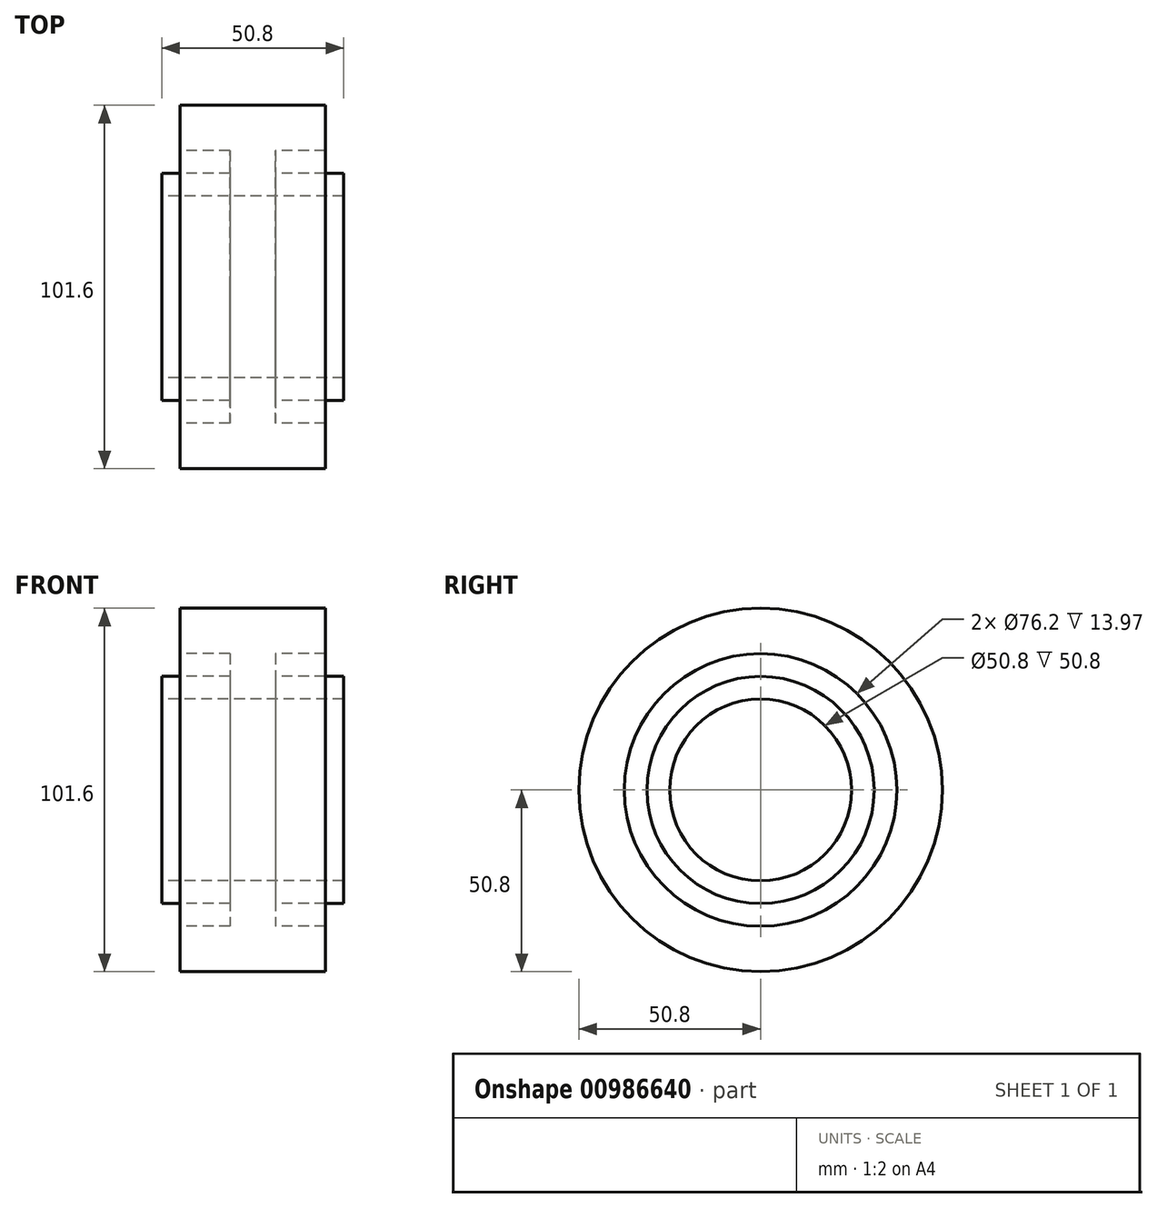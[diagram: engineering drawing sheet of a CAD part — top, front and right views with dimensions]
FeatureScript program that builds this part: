
annotation { "Feature Type Name" : "Feature", "Feature Type Description" : "" }
export const myFeature = defineFeature(function(context is Context, id is Id, definition is map)
    precondition{}
    {
        {
            var Q0;
            Q0=qCreatedBy(makeId("Front.planeOp"),FACE);
            var sketch = newSketch(context, id + "F0", { "sketchPlane" : qUnion([Q0])});
            skLineSegment(sketch, "E0", {"start": v(-79.7, 0) * mm, "end": v(82.55, 0) * mm, "construction": true});
            skLineSegment(sketch, "E1", {"start": v(-25.4, 25.4) * mm, "end": v(25.4, 25.4) * mm});
            skLineSegment(sketch, "E2", {"start": v(25.4, 25.4) * mm, "end": v(25.4, 31.75) * mm});
            skLineSegment(sketch, "E3", {"start": v(25.4, 31.75) * mm, "end": v(6.35, 31.75) * mm});
            skLineSegment(sketch, "E4", {"start": v(6.35, 31.75) * mm, "end": v(6.35, 38.1) * mm});
            skLineSegment(sketch, "E5", {"start": v(6.35, 38.1) * mm, "end": v(20.32, 38.1) * mm});
            skLineSegment(sketch, "E6", {"start": v(20.32, 38.1) * mm, "end": v(20.32, 50.8) * mm});
            skLineSegment(sketch, "E7", {"start": v(20.32, 50.8) * mm, "end": v(-20.32, 50.8) * mm});
            skLineSegment(sketch, "E8", {"start": v(-20.32, 50.8) * mm, "end": v(-20.32, 38.1) * mm});
            skLineSegment(sketch, "E9", {"start": v(-20.32, 38.1) * mm, "end": v(-6.35, 38.1) * mm});
            skLineSegment(sketch, "E10", {"start": v(-6.35, 38.1) * mm, "end": v(-6.35, 31.75) * mm});
            skLineSegment(sketch, "E11", {"start": v(-6.35, 31.75) * mm, "end": v(-25.4, 31.75) * mm});
            skLineSegment(sketch, "E12", {"start": v(-25.4, 31.75) * mm, "end": v(-25.4, 25.4) * mm});
            skLineSegment(sketch, "E13", {"start": v(0, 0) * mm, "end": v(0, 72.7) * mm, "construction": true});
            skSolve(sketch);
        }
        {
            var Q0;
            Q0 = qSketchRegion(id + "F0", true);
            var Q1;
            Q1=sQuery(id+"F0.wireOp",EDGE,"E0");
            revolve(context, id + "F1", {"surfaceOperationType" : NewSurfaceOperationType.NEW, "entities" : qUnion([Q0]), "axis" : qUnion([Q1]), "revolveType" : RevolveType.FULL});
        }
    });
